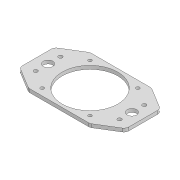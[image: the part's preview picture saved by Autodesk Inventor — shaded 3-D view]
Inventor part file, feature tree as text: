
AUTODESK INVENTOR PART (.ipt)
format: ipt  version: 2020 (Build 240168000, 168)  size: 143,360 bytes
history: native  units: mm
features: mirror x2, other x1, extrude x1
ambient origin geometry x8: Origin, YZ Plane, XZ Plane, XY Plane, X Axis, Y Axis, Z Axis, Center Point
bodies: Body1 (feature_tree)
feature tree (4):
  other  "Sólido1"
  extrude  "Extrusão1"  Depth=65.0mm
  mirror  "Espelhamento1"
  mirror  "Espelhamento3"
